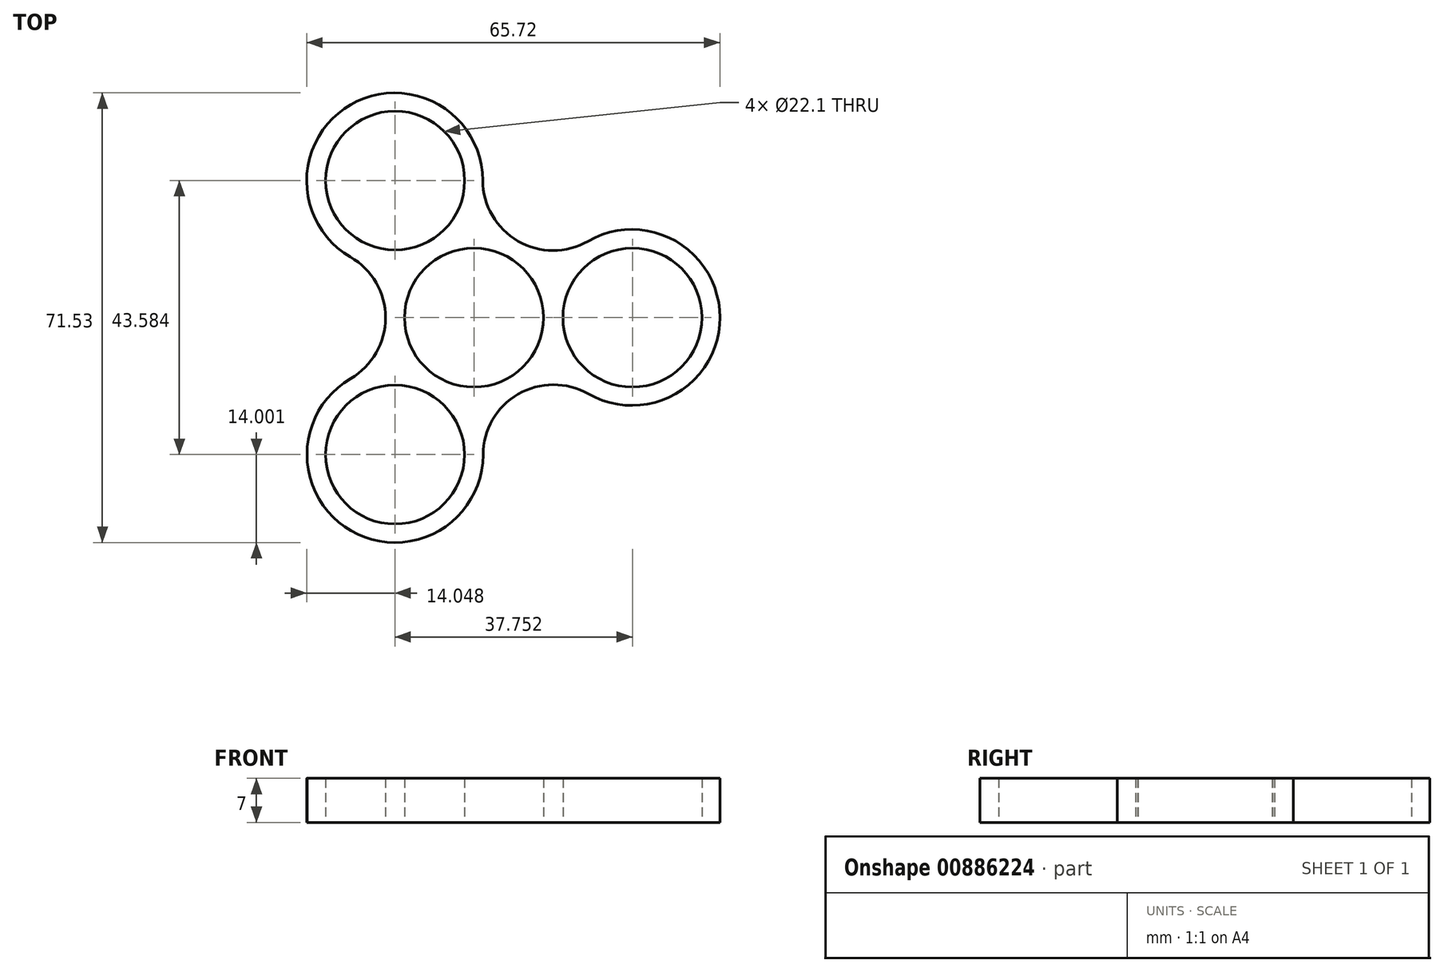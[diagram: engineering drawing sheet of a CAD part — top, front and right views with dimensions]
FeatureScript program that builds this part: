
annotation { "Feature Type Name" : "Feature", "Feature Type Description" : "" }
export const myFeature = defineFeature(function(context is Context, id is Id, definition is map)
    precondition{}
    {
        {
            var Q0;
            Q0=qCreatedBy(makeId("Top.planeOp"),FACE);
            var sketch = newSketch(context, id + "F0", { "sketchPlane" : qUnion([Q0])});
            skCircle(sketch, "E0", {"center": v(0, 0) * mm, "radius": 11.05 * mm});
            skLineSegment(sketch, "E1", {"start": v(0, 0) * mm, "end": v(25.2, 0) * mm, "construction": true});
            skCircle(sketch, "E2", {"center": v(25.2, 0) * mm, "radius": 11.05 * mm});
            skCircle(sketch, "E3", {"center": v(0, 0) * mm, "radius": 25.2 * mm, "construction": true});
            skCircle(sketch, "E4.0", {"center": v(25.2, 0) * mm, "radius": 12.05 * mm});
            skCircle(sketch, "E5.1.0", {"center": v(-12.54, 21.8) * mm, "radius": 12.05 * mm});
            skCircle(sketch, "E5.1.1", {"center": v(-12.54, 21.8) * mm, "radius": 11.05 * mm});
            skCircle(sketch, "E5.2.0", {"center": v(-12.55, -21.78) * mm, "radius": 12.05 * mm});
            skCircle(sketch, "E5.2.1", {"center": v(-12.55, -21.78) * mm, "radius": 11.05 * mm});
            skPoint(sketch, "E5.center", {"position": v(0.04, 0) * mm});
            skLineSegment(sketch, "E6", {"start": v(-12.54, 21.8) * mm, "end": v(12.56, -21.85) * mm, "construction": true});
            skLineSegment(sketch, "E7", {"start": v(-12.55, -21.78) * mm, "end": v(12.56, -21.85) * mm, "construction": true});
            skLineSegment(sketch, "E8", {"start": v(12.56, -21.85) * mm, "end": v(25.2, 0) * mm, "construction": true});
            skLineSegment(sketch, "E9", {"start": v(5.5, -9.58) * mm, "end": v(6, -10.45) * mm, "construction": true});
            skPoint(sketch, "E10", {"position": v(7, -12.18) * mm});
            skCircle(sketch, "E11", {"center": v(-12.55, -21.78) * mm, "radius": 14 * mm});
            skCircle(sketch, "E12.1.0", {"center": v(25.12, 0.03) * mm, "radius": 14 * mm});
            skCircle(sketch, "E12.2.0", {"center": v(-12.6, 21.75) * mm, "radius": 14 * mm});
            skPoint(sketch, "E12.center", {"position": v(-0.01, 0) * mm});
            skArc(sketch, "E13", {"start": v(18.18, -12.13) * mm, "mid": v(7.03, -12.16) * mm, "end": v(1.45, -21.82) * mm});
            skArc(sketch, "E14.1.0", {"start": v(1.4, 21.82) * mm, "mid": v(7, 12.18) * mm, "end": v(18.15, 12.17) * mm});
            skArc(sketch, "E14.2.0", {"start": v(-19.61, -9.7) * mm, "mid": v(-14.07, -0.02) * mm, "end": v(-19.64, 9.65) * mm});
            skSolve(sketch);
        }
        {
            var Q0;
            Q0=makeQuery(id+"F0.imprint","IMPRINT",FACE,{"disambiguationData":[TD([[makeQuery(id+"F0.imprint","IMPRINT",EDGE,{"derivedFrom":sQuery(id+"F0.wireOp",EDGE,"E0")}),-1.0]])]});
            var Q1;
            Q1=makeQuery(id+"F0.imprint","IMPRINT",FACE,{"disambiguationData":[TD([[makeQuery(id+"F0.imprint","IMPRINT",EDGE,{"derivedFrom":sQuery(id+"F0.wireOp",EDGE,"E5.1.0")}),-1.0]])]});
            var Q2;
            Q2=makeQuery(id+"F0.imprint","IMPRINT",FACE,{"disambiguationData":[TD([[makeQuery(id+"F0.imprint","IMPRINT",EDGE,{"derivedFrom":sQuery(id+"F0.wireOp",EDGE,"E5.1.0")}),1.0]])]});
            var Q3;
            Q3=makeQuery(id+"F0.imprint","IMPRINT",FACE,{"disambiguationData":[TD([[makeQuery(id+"F0.imprint","IMPRINT",EDGE,{"derivedFrom":sQuery(id+"F0.wireOp",EDGE,"E5.2.0")}),-1.0]])]});
            var Q4;
            Q4=makeQuery(id+"F0.imprint","IMPRINT",FACE,{"disambiguationData":[TD([[makeQuery(id+"F0.imprint","IMPRINT",EDGE,{"derivedFrom":sQuery(id+"F0.wireOp",EDGE,"E5.2.0")}),1.0]])]});
            var Q5;
            Q5=makeQuery(id+"F0.imprint","IMPRINT",FACE,{"disambiguationData":[TD([[makeQuery(id+"F0.imprint","IMPRINT",EDGE,{"derivedFrom":sQuery(id+"F0.wireOp",EDGE,"E2")}),-1.0]])]});
            var Q6;
            Q6=makeQuery(id+"F0.imprint","IMPRINT",FACE,{"disambiguationData":[TD([[makeQuery(id+"F0.imprint","IMPRINT",EDGE,{"derivedFrom":sQuery(id+"F0.wireOp",EDGE,"E4.0")}),-1.0]])]});
            extrude(context, id + "F1", {"entities" : qUnion([Q0, Q1, Q2, Q3, Q4, Q5, Q6]), "depth" : 7 * mm, "offsetDistance" : 25 * mm});
        }
    });
